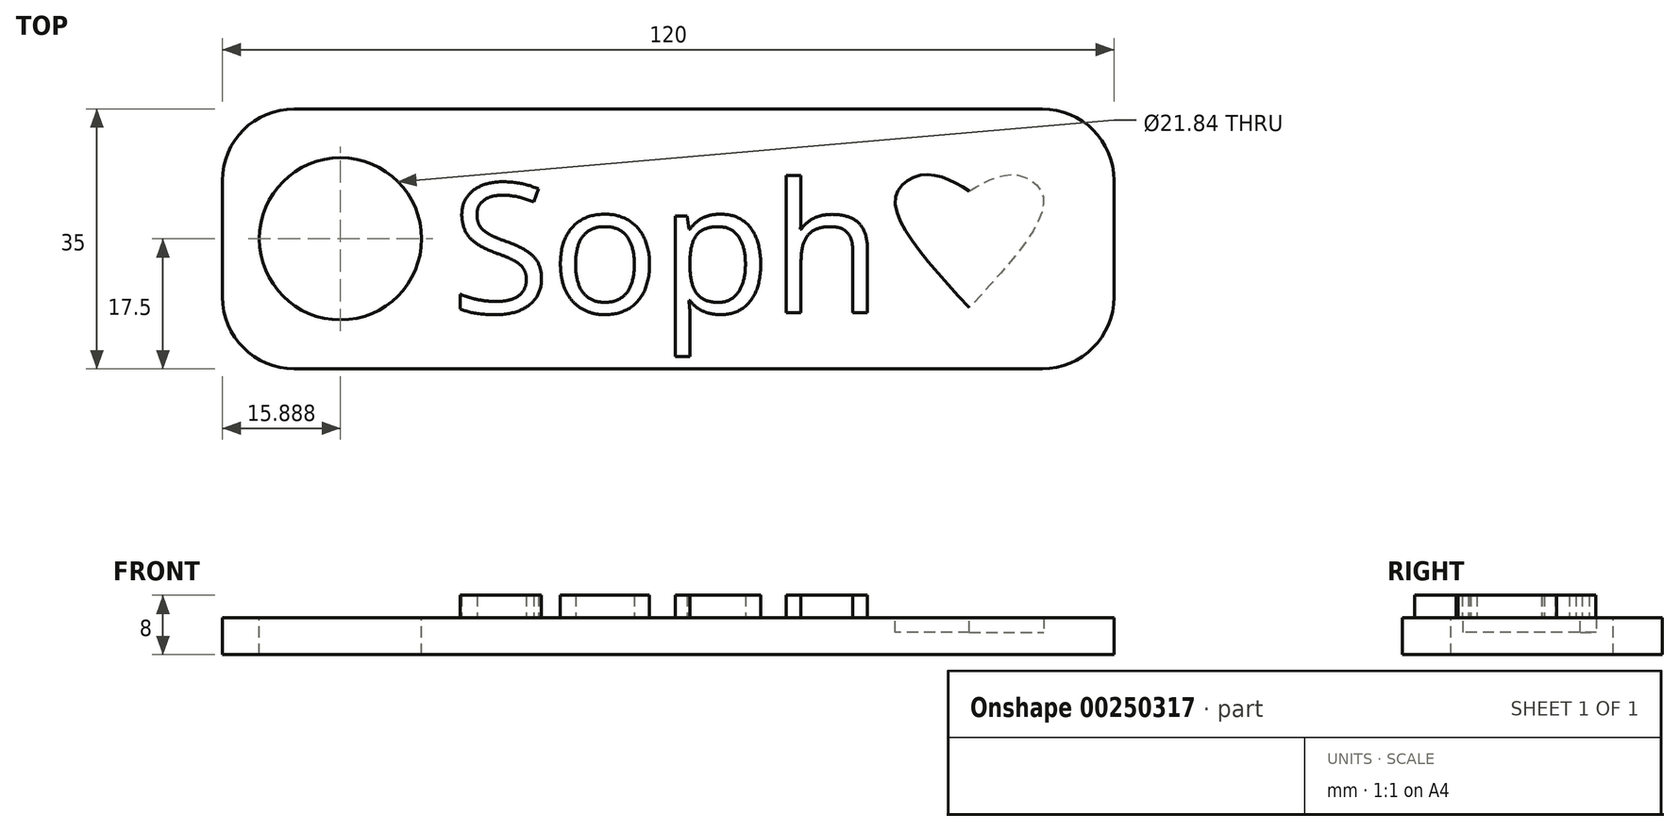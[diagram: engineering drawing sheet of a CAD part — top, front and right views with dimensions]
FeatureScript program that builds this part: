
annotation { "Feature Type Name" : "Feature", "Feature Type Description" : "" }
export const myFeature = defineFeature(function(context is Context, id is Id, definition is map)
    precondition{}
    {
        {
            var Q0;
            Q0=qCreatedBy(makeId("Top.planeOp"),FACE);
            var sketch = newSketch(context, id + "F0", { "sketchPlane" : qUnion([Q0])});
            skLineSegment(sketch, "E0.bottom", {"start": v(-60, 17.5) * mm, "end": v(60, 17.5) * mm});
            skLineSegment(sketch, "E0.top", {"start": v(-60, -17.5) * mm, "end": v(60, -17.5) * mm});
            skLineSegment(sketch, "E0.left", {"start": v(-60, 17.5) * mm, "end": v(-60, -17.5) * mm});
            skLineSegment(sketch, "E0.right", {"start": v(60, 17.5) * mm, "end": v(60, -17.5) * mm});
            skPoint(sketch, "E0.middle", {"position": v(0, 0) * mm});
            skSolve(sketch);
        }
        {
            var Q0;
            Q0 = qSketchRegion(id + "F0", true);
            extrude(context, id + "F1", {"entities" : qUnion([Q0]), "depth" : 5 * mm});
        }
        {
            var Q0;
            Q0=makeQuery(id+"F1.opExtrude","CAP_FACE",FACE,{"disambiguationData":[OSD([sQuery(id+"F0.wireOp",EDGE,"E0.bottom"),sQuery(id+"F0.wireOp",EDGE,"E0.top"),sQuery(id+"F0.wireOp",EDGE,"E0.left"),sQuery(id+"F0.wireOp",EDGE,"E0.right")])],"isStart":false});
            var sketch = newSketch(context, id + "F2", { "sketchPlane" : qUnion([Q0])});
            skCircle(sketch, "E1", {"center": v(-44.11, 0) * mm, "radius": 10.92 * mm});
            skSolve(sketch);
        }
        {
            var Q0;
            Q0=makeQuery(id+"F1.opExtrude","SWEPT_EDGE",EDGE,{"disambiguationData":[OSD([sQuery(id+"F0.wireOp",EDGE,"E0.bottom"),sQuery(id+"F0.wireOp",EDGE,"E0.right")])]});
            var Q1;
            Q1=makeQuery(id+"F1.opExtrude","SWEPT_EDGE",EDGE,{"disambiguationData":[OSD([sQuery(id+"F0.wireOp",EDGE,"E0.top"),sQuery(id+"F0.wireOp",EDGE,"E0.right")])]});
            var Q2;
            Q2=makeQuery(id+"F1.opExtrude","SWEPT_EDGE",EDGE,{"disambiguationData":[OSD([sQuery(id+"F0.wireOp",EDGE,"E0.top"),sQuery(id+"F0.wireOp",EDGE,"E0.left")])]});
            var Q3;
            Q3=makeQuery(id+"F1.opExtrude","SWEPT_EDGE",EDGE,{"disambiguationData":[OSD([sQuery(id+"F0.wireOp",EDGE,"E0.bottom"),sQuery(id+"F0.wireOp",EDGE,"E0.left")])]});
            fillet(context, id + "F3", {"entities" : qUnion([Q0, Q1, Q2, Q3]), "radius" : 9.66 * mm, "tangentPropagation" : true, "allowEdgeOverflow" : false});
        }
        {
            var Q0;
            Q0 = qSketchRegion(id + "F2", true);
            extrude(context, id + "F4", {"entities" : qUnion([Q0]), "operationType" : NewBodyOperationType.REMOVE, "oppositeDirection" : true, "depth" : 25 * mm});
        }
        {
            var Q0;
            Q0=makeQuery(id+"F1.opExtrude","CAP_FACE",FACE,{"disambiguationData":[OSD([sQuery(id+"F0.wireOp",EDGE,"E0.bottom"),sQuery(id+"F0.wireOp",EDGE,"E0.top"),sQuery(id+"F0.wireOp",EDGE,"E0.left"),sQuery(id+"F0.wireOp",EDGE,"E0.right")])],"isStart":false});
            var sketch = newSketch(context, id + "F5", { "sketchPlane" : qUnion([Q0])});
            skText(sketch, "E2", { "text": "Soph", "fontName": "OpenSans-Regular.ttf"});
            skFitSpline(sketch, "E3", {"points": [v(40.53, 6.45) * mm, v(34.45, 8.64) * mm, v(30.57, 5.43) * mm, v(40.53, -9.26) * mm], "startDerivative": vector(-21.39, 12.6) * mm, "endDerivative": vector(33.33, -36.03) * mm});
            skFitSpline(sketch, "E4.MirrorCS", {"points": [v(40.53, 6.45) * mm, v(46.6, 8.64) * mm, v(50.49, 5.43) * mm, v(40.53, -9.26) * mm], "startDerivative": vector(21.39, 12.6) * mm, "endDerivative": vector(-33.33, -36.03) * mm});
            const initialGuessF5  = {"E2": [-0.02614, -0.0078, 1, 0, 0.01605]};
            skSetInitialGuess(sketch, initialGuessF5);
            skSolve(sketch);
        }
        {
            var Q0;
            Q0=makeQuery(id+"F5.imprint","IMPRINT",FACE,{"disambiguationData":[TD([[makeQuery(id+"F5.imprint","IMPRINT",EDGE,{"derivedFrom":sQuery(id+"F5.wireOp",EDGE,"E3")}),1.0]])]});
            var Q1;
            Q1=sQuery(id+"F5.wireOp",EDGE,"E4.MirrorCS");
            var Q2;
            Q2=sQuery(id+"F5.wireOp",EDGE,"E3");
            extrude(context, id + "F6", {"entities" : qUnion([Q0]), "operationType" : NewBodyOperationType.REMOVE, "surfaceEntities" : qUnion([Q1, Q2]), "oppositeDirection" : true, "depth" : 2 * mm});
        }
        {
            var Q0;
            Q0=makeQuery(id+"F1.opExtrude","CAP_FACE",FACE,{"disambiguationData":[OSD([sQuery(id+"F0.wireOp",EDGE,"E0.bottom"),sQuery(id+"F0.wireOp",EDGE,"E0.top"),sQuery(id+"F0.wireOp",EDGE,"E0.left"),sQuery(id+"F0.wireOp",EDGE,"E0.right")])],"isStart":false});
            var sketch = newSketch(context, id + "F7", { "sketchPlane" : qUnion([Q0])});
            skText(sketch, "E5", { "text": "Soph", "fontName": "OpenSans-Regular.ttf"});
            const initialGuessF7  = {"E5": [-0.02927, -0.00997, 1, 0, 0.01756]};
            skSetInitialGuess(sketch, initialGuessF7);
            skSolve(sketch);
        }
        {
            var Q0;
            Q0 = qSketchRegion(id + "F7", true);
            extrude(context, id + "F8", {"entities" : qUnion([Q0]), "operationType" : NewBodyOperationType.ADD, "depth" : 3 * mm});
        }
    });
